# Revit family: Storage-Teknion-EMCC_Low_Double_Cabinet_With_Cubby-R2016
name_source: partatom
category: Furniture
revit_build: Autodesk Revit 2018 (Build: 20190510_1515(x64)
units: mm (PartAtom-declared; Revit-internal decimal feet)

## family parameters
Always vertical = Yes
Cut with Voids When Loaded = No
OmniClass Number = 23.40.20.00
OmniClass Title = General Furniture and Specialties
Room Calculation Point = No
Shared = Yes
Work Plane-Based = No

## types (4) — shared parameters
Assembly Code = E2020200
Manufacturer = Teknion
Manufacturer Fax = 416.661.4586
Part Number = EMCC
Product Documentation Link = https://assets.teknion.com
Product Line = Emote
Product Page URL = https://www.teknion.com
Series = Emote
Sustainability Data = https://www.teknion.com
URL = www.teknion.com
Unit Weight URL = http://www.teknion.com
Warranty = http://www.teknion.com

## per-type parameters (varying)
| type | Center Double Doors | Center Full Height Drawer | Center Open | Center Partial Height Drawer | Center Single Door | Description | Model |
| Center Open Drawer Configuration | No | No | Yes | No | No | Low Double Cabinet With Cubby, Center Open Drawer Configuration , 73.25" Width | EMCC__OP73_ |
| Center Double Doors Drawer Configuration | Yes | No | No | No | No | Low Double Cabinet With Cubby, Center Double Doors Drawer Configuration , 73.25" Width | EMCC__CL73_ |
| Center Partial Height Drawer Configuration | No | No | No | Yes | Yes | Low Double Cabinet With Cubby, Center Partial Height Drawer Configuration , 73.25" Width | EMCC__PD73_ |
| Center Full Height Drawer Configuration | No | Yes | No | No | Yes | Low Double Cabinet With Cubby, Center Full Height Drawer Configuration , 73.25" Width | EMCC__FD73_ |

## geometry (parser evidence)
native form markers: Blend x43, Sweep x2
no freeform markers — native parametric forms only
